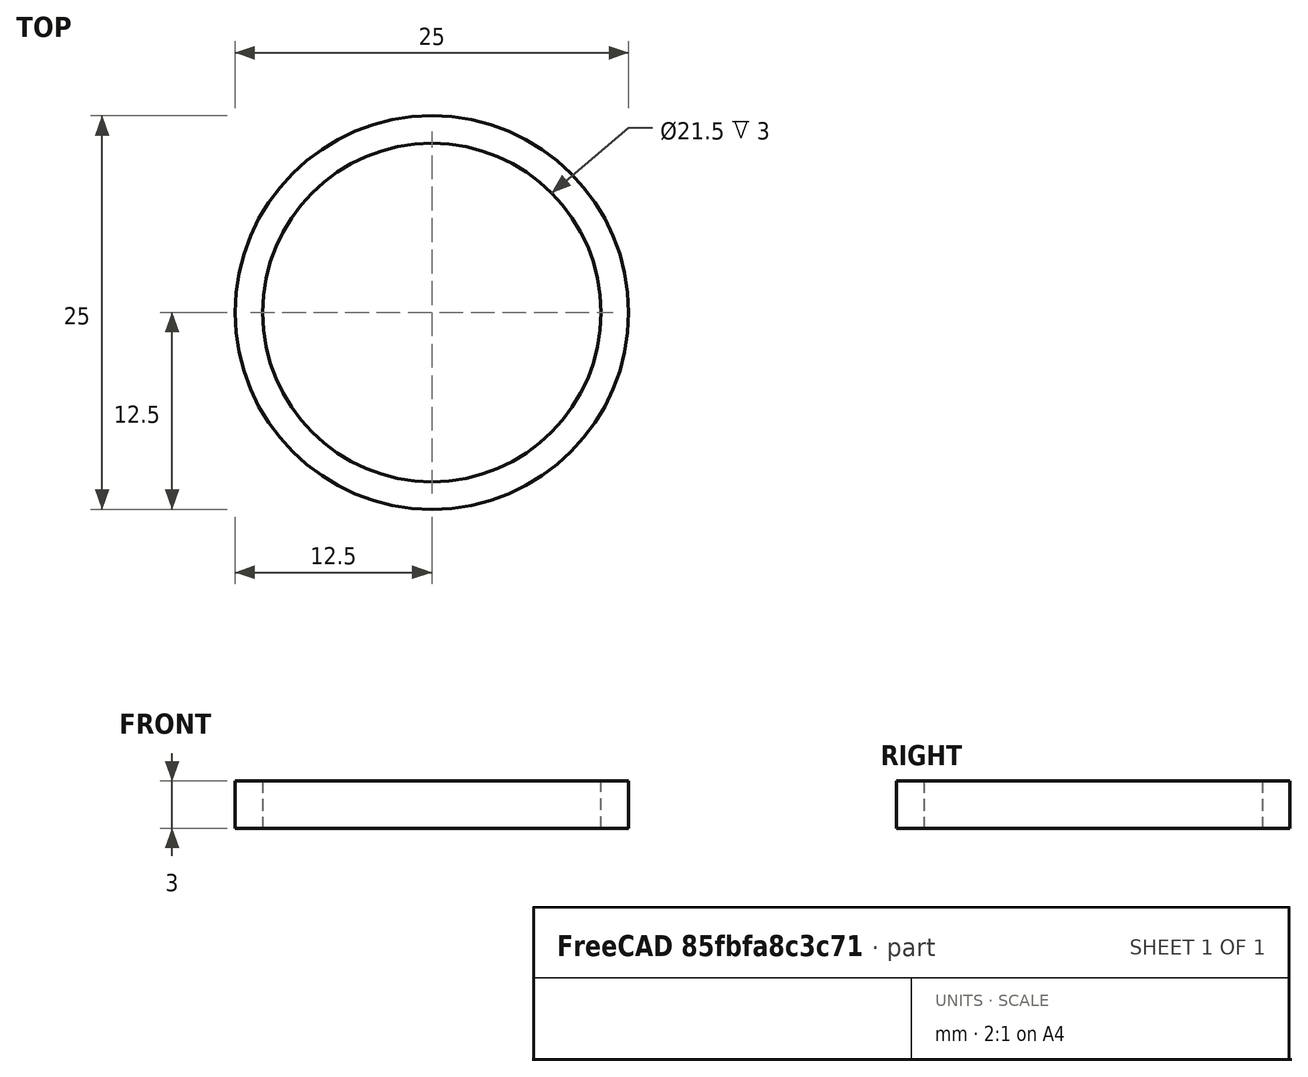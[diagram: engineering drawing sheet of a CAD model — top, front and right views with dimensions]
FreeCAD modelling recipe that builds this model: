
FCSTD DOCUMENT  (FreeCAD 0.20R29603 (Git))
Label: LaserFixCircle
License: All rights reserved
LicenseURL: http://en.wikipedia.org/wiki/All_rights_reserved
objects: Sketcher::SketchObject×1, PartDesign::Pad×1, PartDesign::Body×1
note: 4 computed .brp shape members not serialized (recipe doc carries the construction recipe); baked Part::Feature solids carry a one-line shape summary decoded from their .brp

FEATURE [Sketcher::SketchObject] Sketch
  FullyConstrained = true
  MapMode = 5
  Support = -> [XY_Plane]
  sketch-geometry (2):
    g0: Circle CenterX=0 CenterY=0 CenterZ=0 NormalX=0 NormalY=0 NormalZ=1 AngleXU=0 Radius=10.75
    g1: Circle CenterX=0 CenterY=0 CenterZ=0 NormalX=0 NormalY=0 NormalZ=1 AngleXU=0 Radius=12.5
  constraints (4):
    c: Coincident(g0,g-1)
    c: Coincident(g1,g0)
    c: Diameter(g0) = 21.5
    c: Diameter(g1) = 25
FEATURE [PartDesign::Pad] Pad
  Direction = (0,0,1)
  Length = 3
  Length2 = 10
  Profile = -> Sketch
  ReferenceAxis = -> Sketch [N_Axis]
  Type = 0
FEATURE [PartDesign::Body] Body
  Group = -> [Sketch,Pad]
  Origin = -> Origin
  Tip = -> Pad
